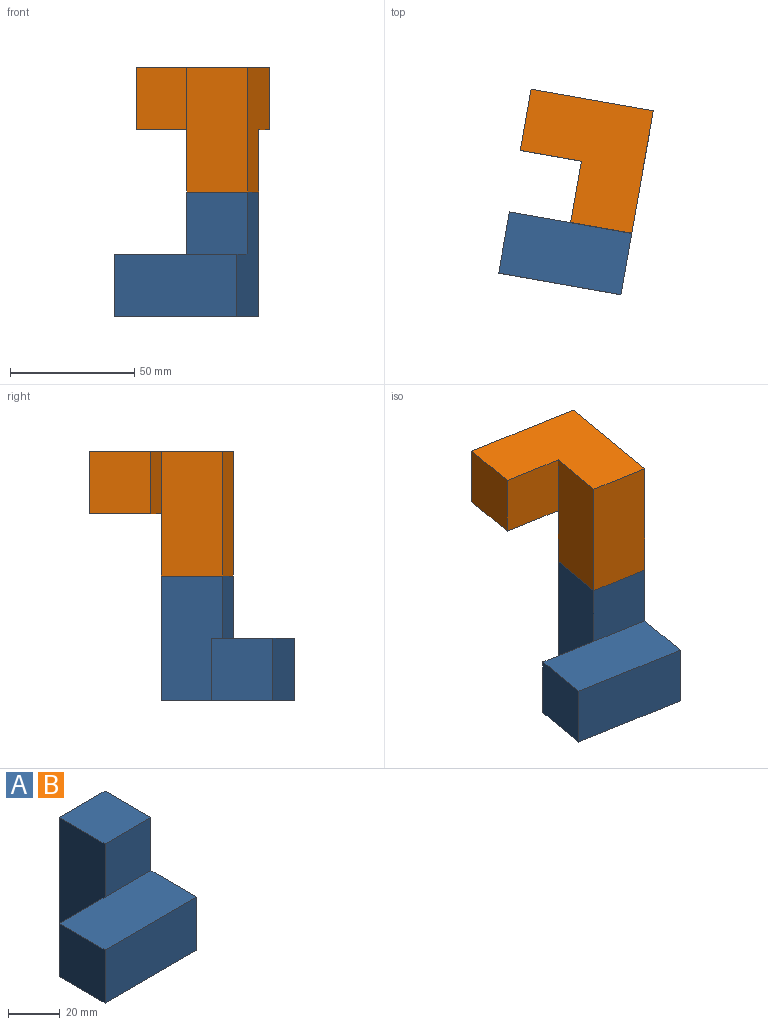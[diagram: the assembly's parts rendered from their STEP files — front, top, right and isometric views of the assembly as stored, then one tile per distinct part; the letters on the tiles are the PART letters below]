
ASSEMBLY  parts=2 mates=1
PART A: 10 faces, bbox 50x50x50 mm
  f0: plane 50x25mm, normal (0,0,1), area 1250mm2, adj f1,f2,f3,f5,f8
  f1: plane 25x25mm, normal (0,1,0), area 625mm2, adj f0,f2,f4,f6
  f2: plane 25x25mm, normal (-1,0,0), area 625mm2, adj f0,f1,f3,f4
  f3: plane 50x25mm, normal (0,-1,0), area 1250mm2, adj f0,f2,f4,f5
  f4: plane 50x50mm, normal (0,0,-1), area 1875mm2, adj f1,f2,f3,f5,f6,f7
  f5: plane 50x50mm, normal (1,0,0), area 1875mm2, adj f0,f3,f4,f7,f8,f9
  f6: plane 50x25mm, normal (-1,0,0), area 1250mm2, adj f1,f4,f7,f8,f9
  f7: plane 50x25mm, normal (0,1,0), area 1250mm2, adj f4,f5,f6,f9
  f8: plane 25x25mm, normal (0,-1,0), area 625mm2, adj f0,f5,f6,f9
  f9: plane 25x25mm, normal (0,0,1), area 625mm2, adj f5,f6,f7,f8
PART B: same geometry as A
PLACE A rot(axis=(0,0,-1),10deg) t=(44.6,4.11,21.11)mm
PLACE B rot(axis=(1,-0.09,0),180deg) t=(57.63,77.97,121.11)mm
MATE revolute B.f9 <-> A.f9  axis (0,0,-1) through (88.05,34.53,71.11)mm
